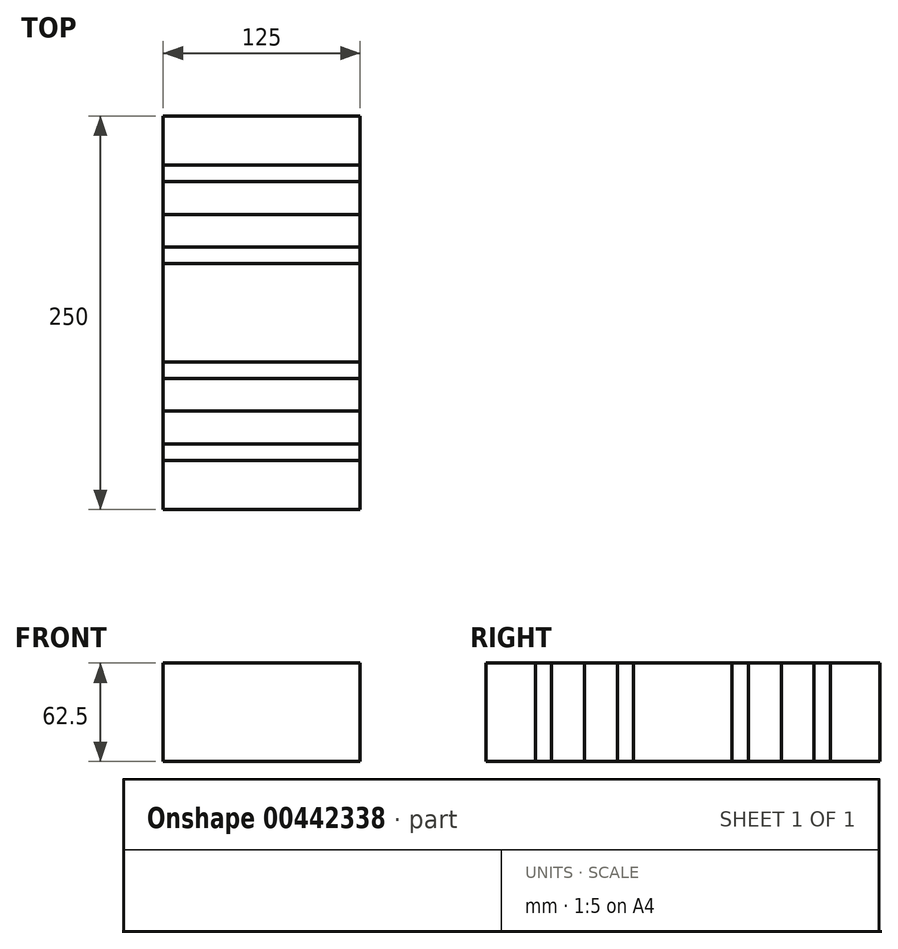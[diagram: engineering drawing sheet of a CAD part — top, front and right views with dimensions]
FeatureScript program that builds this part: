
annotation { "Feature Type Name" : "Feature", "Feature Type Description" : "" }
export const myFeature = defineFeature(function(context is Context, id is Id, definition is map)
    precondition{}
    {
        {
            var Q0;
            Q0=qCreatedBy(makeId("Front.planeOp"),FACE);
            var sketch = newSketch(context, id + "F0", { "sketchPlane" : qUnion([Q0])});
            skLineSegment(sketch, "E0.bottom", {"start": v(62.5, 31.25) * mm, "end": v(-62.5, 31.25) * mm});
            skLineSegment(sketch, "E0.top", {"start": v(62.5, -31.25) * mm, "end": v(-62.5, -31.25) * mm});
            skLineSegment(sketch, "E0.left", {"start": v(62.5, 31.25) * mm, "end": v(62.5, -31.25) * mm});
            skLineSegment(sketch, "E0.right", {"start": v(-62.5, 31.25) * mm, "end": v(-62.5, -31.25) * mm});
            skPoint(sketch, "E0.middle", {"position": v(0, 0) * mm});
            skSolve(sketch);
        }
        {
            var Q0;
            Q0=makeQuery(id+"F0.imprint","IMPRINT",FACE,{"disambiguationData":[TD([[makeQuery(id+"F0.imprint","IMPRINT",EDGE,{"derivedFrom":sQuery(id+"F0.wireOp",EDGE,"E0.bottom")}),1.0]])]});
            extrude(context, id + "F1", {"entities" : qUnion([Q0]), "endBound" : BoundingType.SYMMETRIC, "depth" : 250 * mm});
        }
        {
            var Q0;
            Q0=qSketchRegion(id+"F0",true);
            extrude(context, id + "F2", {"entities" : qUnion([Q0]), "endBound" : BoundingType.SYMMETRIC, "depth" : 125 * mm});
        }
        {
            var Q0;
            Q0=makeQuery(id+"F0.imprint","IMPRINT",FACE,{"disambiguationData":[TD([[makeQuery(id+"F0.imprint","IMPRINT",EDGE,{"derivedFrom":sQuery(id+"F0.wireOp",EDGE,"E0.bottom")}),1.0]])]});
            extrude(context, id + "F3", {"entities" : qUnion([Q0]), "endBound" : BoundingType.SYMMETRIC, "depth" : (250 * 3 / 4) * mm});
        }
        {
            var Q0;
            Q0=makeQuery(id+"F0.imprint","IMPRINT",FACE,{"disambiguationData":[TD([[makeQuery(id+"F0.imprint","IMPRINT",EDGE,{"derivedFrom":sQuery(id+"F0.wireOp",EDGE,"E0.bottom")}),1.0]])]});
            extrude(context, id + "F4", {"entities" : qUnion([Q0]), "endBound" : BoundingType.SYMMETRIC, "depth" : (250 / 4) * mm});
        }
        {
            var Q0;
            Q0=makeQuery(id+"F0.imprint","IMPRINT",FACE,{"disambiguationData":[TD([[makeQuery(id+"F0.imprint","IMPRINT",EDGE,{"derivedFrom":sQuery(id+"F0.wireOp",EDGE,"E0.bottom")}),1.0]])]});
            extrude(context, id + "F5", {"entities" : qUnion([Q0]), "endBound" : BoundingType.SYMMETRIC, "depth" : 250 * 2 / 3 * mm});
        }
        {
            var Q0;
            Q0=makeQuery(id+"F0.imprint","IMPRINT",FACE,{"disambiguationData":[TD([[makeQuery(id+"F0.imprint","IMPRINT",EDGE,{"derivedFrom":sQuery(id+"F0.wireOp",EDGE,"E0.bottom")}),1.0]])]});
            extrude(context, id + "F6", {"entities" : qUnion([Q0]), "endBound" : BoundingType.SYMMETRIC, "depth" : (250 / 3) * mm});
        }
    });
